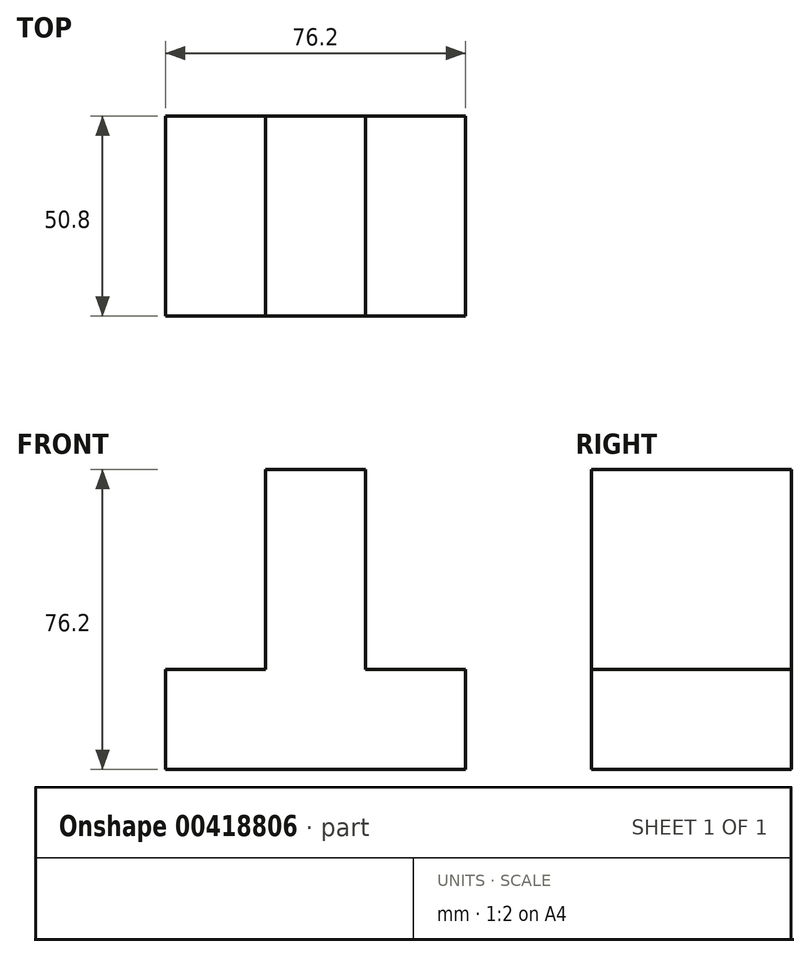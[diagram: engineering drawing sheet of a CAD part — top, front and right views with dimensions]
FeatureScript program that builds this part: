
annotation { "Feature Type Name" : "Feature", "Feature Type Description" : "" }
export const myFeature = defineFeature(function(context is Context, id is Id, definition is map)
    precondition{}
    {
        {
            var Q0;
            Q0=qCreatedBy(makeId("Front.planeOp"),FACE);
            var sketch = newSketch(context, id + "F0", { "sketchPlane" : qUnion([Q0])});
            skLineSegment(sketch, "E0", {"start": v(-64.92, 0) * mm, "end": v(11.28, 0) * mm});
            skLineSegment(sketch, "E1", {"start": v(11.28, 0) * mm, "end": v(11.28, 25.4) * mm});
            skLineSegment(sketch, "E2", {"start": v(11.28, 25.4) * mm, "end": v(-14.12, 25.4) * mm});
            skLineSegment(sketch, "E3", {"start": v(-14.12, 25.4) * mm, "end": v(-14.12, 76.2) * mm});
            skLineSegment(sketch, "E4", {"start": v(-14.12, 76.2) * mm, "end": v(-39.52, 76.2) * mm});
            skLineSegment(sketch, "E5", {"start": v(-39.52, 76.2) * mm, "end": v(-39.52, 25.4) * mm});
            skLineSegment(sketch, "E6", {"start": v(-39.52, 25.4) * mm, "end": v(-64.92, 25.4) * mm});
            skLineSegment(sketch, "E7", {"start": v(-64.92, 25.4) * mm, "end": v(-64.92, 0) * mm});
            skSolve(sketch);
        }
        {
            var Q0;
            Q0 = qSketchRegion(id + "F0", true);
            extrude(context, id + "F1", {"entities" : qUnion([Q0]), "depth" : 50.8 * mm});
        }
    });
